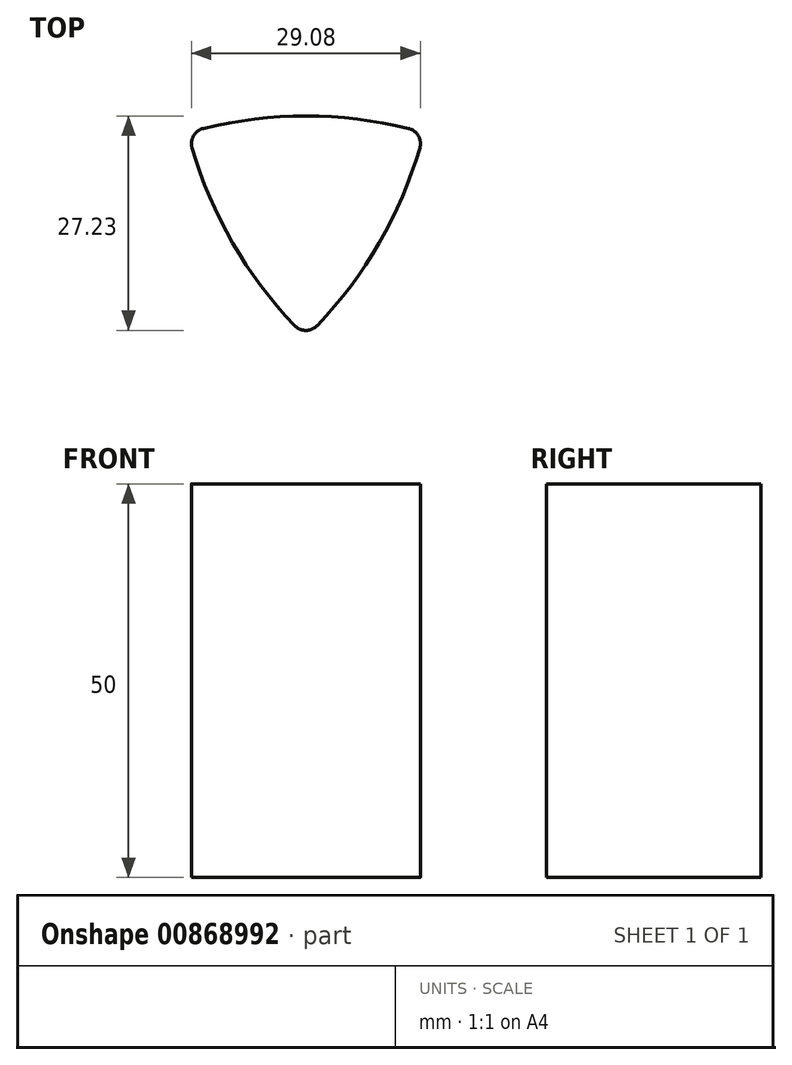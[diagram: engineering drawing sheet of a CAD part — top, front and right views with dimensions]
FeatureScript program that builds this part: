
annotation { "Feature Type Name" : "Feature", "Feature Type Description" : "" }
export const myFeature = defineFeature(function(context is Context, id is Id, definition is map)
    precondition{}
    {
        {
            var Q0;
            Q0=qCreatedBy(makeId("Top.planeOp"),FACE);
            var sketch = newSketch(context, id + "F0", { "sketchPlane" : qUnion([Q0])});
            skLineSegment(sketch, "E0.0", {"start": v(0, -13.48) * mm, "end": v(-15, 12.5) * mm, "construction": true});
            skLineSegment(sketch, "E0.1", {"start": v(-15, 12.5) * mm, "end": v(15, 12.5) * mm, "construction": true});
            skLineSegment(sketch, "E0.2", {"start": v(15, 12.5) * mm, "end": v(0, -13.48) * mm, "construction": true});
            skArc(sketch, "E1", {"start": v(15, 12.5) * mm, "mid": v(0, 14.59) * mm, "end": v(-15, 12.5) * mm});
            skArc(sketch, "E2", {"start": v(0, -13.48) * mm, "mid": v(9.3, -1.53) * mm, "end": v(15, 12.5) * mm});
            skArc(sketch, "E3", {"start": v(-15, 12.5) * mm, "mid": v(-9.3, -1.53) * mm, "end": v(0, -13.48) * mm});
            skSolve(sketch);
        }
        {
            var Q0;
            Q0 = qSketchRegion(id + "F0", true);
            extrude(context, id + "F1", {"entities" : qUnion([Q0]), "depth" : 50 * mm, "offsetDistance" : 25 * mm});
        }
        {
            var Q0;
            Q0=makeQuery(id+"F1.opExtrude","SWEPT_EDGE",EDGE,{"disambiguationData":[OSD([sQuery(id+"F0.wireOp",EDGE,"E2"),sQuery(id+"F0.wireOp",EDGE,"E3")])]});
            var Q1;
            Q1=makeQuery(id+"F1.opExtrude","SWEPT_EDGE",EDGE,{"disambiguationData":[OSD([sQuery(id+"F0.wireOp",EDGE,"E1"),sQuery(id+"F0.wireOp",EDGE,"E2")])]});
            var Q2;
            Q2=makeQuery(id+"F1.opExtrude","SWEPT_EDGE",EDGE,{"disambiguationData":[OSD([sQuery(id+"F0.wireOp",EDGE,"E1"),sQuery(id+"F0.wireOp",EDGE,"E3")])]});
            fillet(context, id + "F2", {"entities" : qUnion([Q0, Q1, Q2]), "radius" : 2 * mm, "tangentPropagation" : true, "allowEdgeOverflow" : false});
        }
    });
